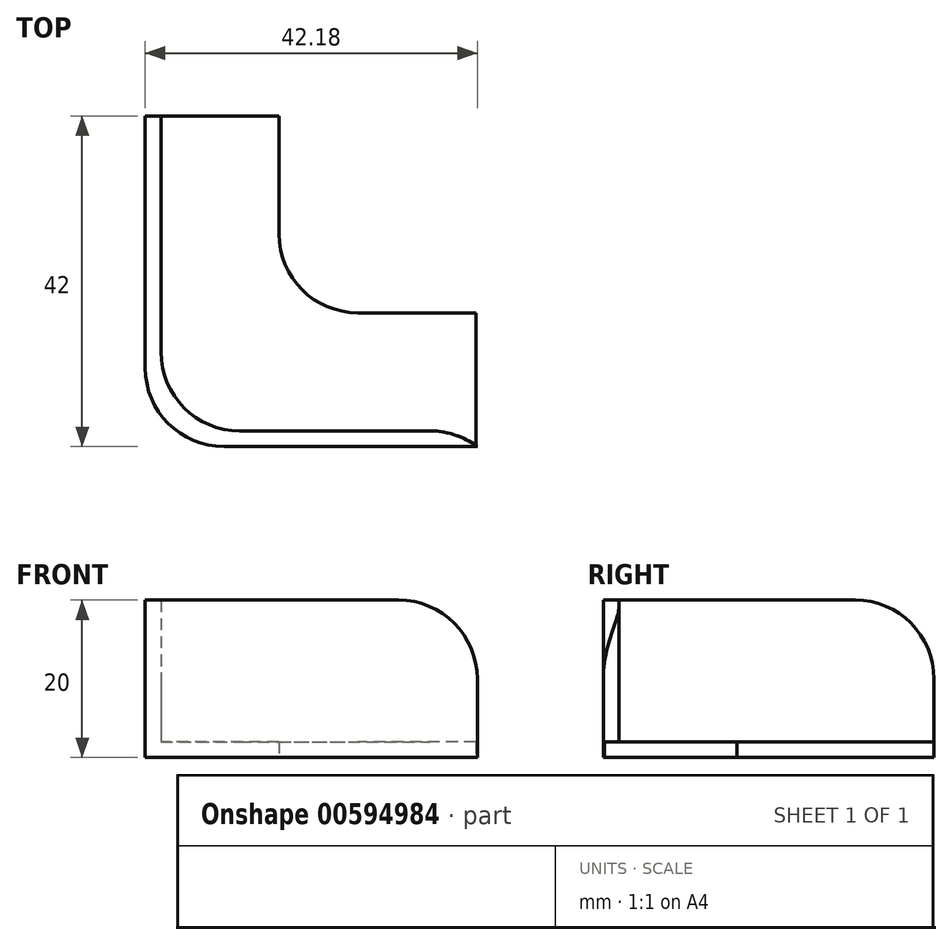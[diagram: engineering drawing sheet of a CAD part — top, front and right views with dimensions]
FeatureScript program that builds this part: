
annotation { "Feature Type Name" : "Feature", "Feature Type Description" : "" }
export const myFeature = defineFeature(function(context is Context, id is Id, definition is map)
    precondition{}
    {
        {
            var Q0;
            Q0=qCreatedBy(makeId("Top.planeOp"),FACE);
            var sketch = newSketch(context, id + "F0", { "sketchPlane" : qUnion([Q0])});
            skLineSegment(sketch, "E0", {"start": v(0, 40) * mm, "end": v(0, 0) * mm});
            skLineSegment(sketch, "E1", {"start": v(0, 0) * mm, "end": v(40, 0) * mm});
            skLineSegment(sketch, "E2", {"start": v(40, 0) * mm, "end": v(40, 15) * mm});
            skLineSegment(sketch, "E3", {"start": v(40, 15) * mm, "end": v(15, 15) * mm});
            skLineSegment(sketch, "E4", {"start": v(15, 15) * mm, "end": v(15, 40) * mm});
            skLineSegment(sketch, "E5", {"start": v(15, 40) * mm, "end": v(0, 40) * mm});
            skSolve(sketch);
        }
        {
            var Q0;
            Q0=makeQuery(id+"F0.imprint","IMPRINT",FACE,{"disambiguationData":[TD([[makeQuery(id+"F0.imprint","IMPRINT",EDGE,{"derivedFrom":sQuery(id+"F0.wireOp",EDGE,"E0")}),1.0]])]});
            extrude(context, id + "F1", {"entities" : qUnion([Q0]), "depth" : 2 * mm, "offsetDistance" : 25 * mm});
        }
        {
            var Q0;
            Q0=qCreatedBy(makeId("Top.planeOp"),FACE);
            var sketch = newSketch(context, id + "F2", { "sketchPlane" : qUnion([Q0])});
            skLineSegment(sketch, "E6", {"start": v(0, 40) * mm, "end": v(-2, 40) * mm});
            skLineSegment(sketch, "E7", {"start": v(-2, 40) * mm, "end": v(-2, -2) * mm});
            skLineSegment(sketch, "E8", {"start": v(-2, -2) * mm, "end": v(40.18, -2) * mm});
            skLineSegment(sketch, "E9", {"start": v(40.18, -2) * mm, "end": v(40.18, 0) * mm});
            skLineSegment(sketch, "E10", {"start": v(40.18, 0) * mm, "end": v(0, 0) * mm});
            skLineSegment(sketch, "E11", {"start": v(0, 0) * mm, "end": v(0, 40) * mm});
            skLineSegment(sketch, "E12", {"start": v(0, 40) * mm, "end": v(0, 0) * mm});
            skSolve(sketch);
        }
        {
            var Q0;
            Q0 = qSketchRegion(id + "F2", true);
            extrude(context, id + "F3", {"entities" : qUnion([Q0]), "operationType" : NewBodyOperationType.ADD, "depth" : 20 * mm, "offsetDistance" : 25 * mm});
        }
        {
            var Q0;
            Q0=makeQuery(id+"F3.opExtrude","SWEPT_EDGE",EDGE,{"disambiguationData":[OSD([sQuery(id+"F2.wireOp",EDGE,"E10"),sQuery(id+"F2.wireOp",EDGE,"E12")])]});
            var Q1;
            Q1=makeQuery(id+"F1.opExtrude","SWEPT_EDGE",EDGE,{"disambiguationData":[OSD([sQuery(id+"F0.wireOp",EDGE,"E3"),sQuery(id+"F0.wireOp",EDGE,"E4")])]});
            var Q2;
            Q2=makeQuery(id+"F3.opExtrude","SWEPT_EDGE",EDGE,{"disambiguationData":[OSD([sQuery(id+"F2.wireOp",EDGE,"E7"),sQuery(id+"F2.wireOp",EDGE,"E8")])]});
            var Q3;
            Q3=makeQuery(id+"F3.opExtrude","CAP_EDGE",EDGE,{"disambiguationData":[OSD([sQuery(id+"F2.wireOp",EDGE,"E6")])],"isStart":false});
            var Q4;
            Q4=makeQuery(id+"F3.opExtrude","CAP_EDGE",EDGE,{"disambiguationData":[OSD([sQuery(id+"F2.wireOp",EDGE,"E9")])],"isStart":false});
            fillet(context, id + "F4", {"entities" : qUnion([Q0, Q1, Q2, Q3, Q4]), "radius" : 10 * mm, "tangentPropagation" : true, "allowEdgeOverflow" : false});
        }
    });
